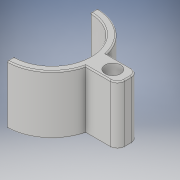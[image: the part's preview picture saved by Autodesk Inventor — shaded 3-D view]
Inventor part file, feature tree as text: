
AUTODESK INVENTOR PART (.ipt)
format: ipt  version: 2019.4 (Build 234330000, 330)  size: 182,784 bytes
history: native  units: in
note: dims shown in document units (in); Inventor stores cm internally (conversion verified against a paired STEP export)
features: extrude x3, sketch x2, fillet x2, hole x1
ambient origin geometry x8: Origin, YZ Plane, XZ Plane, XY Plane, X Axis, Y Axis, Z Axis, Center Point
bodies: Solid1 (feature_tree)
feature tree (8):
  sketch  "Sketch1"  dims[d0=1.3in d1=1.55in]
  extrude  "Extrusion1"  Depth=1.55in
  extrude  "Extrusion2"  Depth=0.02in TaperAngle=0.0deg
  extrude  "Extrusion3"  Depth=0.02in TaperAngle=0.0deg
  hole  "Hole1"  [1 undecoded]
  fillet  "Fillet1"  Radius=0.02in
  fillet  "Fillet2"  [1 undecoded]
  sketch  "Sketch2"  dims[d2=1.0in d3=0.0in d4=1.0in d5=0.0in d6=1.0in d7=0.0in d8=0.266in d9=0.25in d10=0.507in d11=0.25in d12=0.5635in d13=1.0in d14=0.8108in d15=0.125in d16=0.02in]
note: 2 required parameter values undecoded (feature->parameter linkage not recoverable at this tier; creation-order binding heuristic only, values carry confidence <= 0.55)
